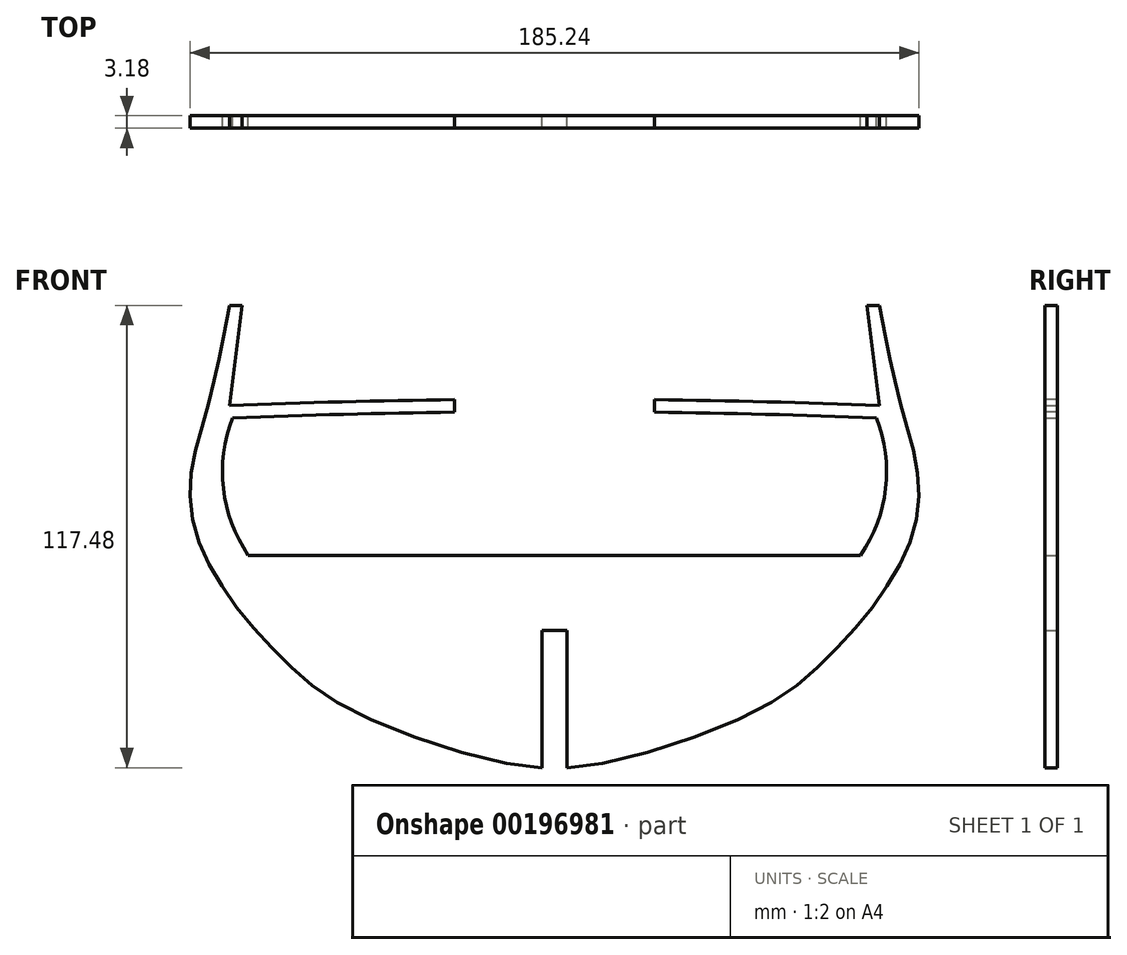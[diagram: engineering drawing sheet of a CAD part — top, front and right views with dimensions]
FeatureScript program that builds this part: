
annotation { "Feature Type Name" : "Feature", "Feature Type Description" : "" }
export const myFeature = defineFeature(function(context is Context, id is Id, definition is map)
    precondition{}
    {
        {
            var Q0;
            Q0=qCreatedBy(makeId("Front.planeOp"),FACE);
            var sketch = newSketch(context, id + "F0", { "sketchPlane" : qUnion([Q0])});
            skLineSegment(sketch, "E0", {"start": v(0, 0) * mm, "end": v(0, -53.97) * mm, "construction": true});
            skLineSegment(sketch, "E1", {"start": v(0, 0) * mm, "end": v(0, 34.93) * mm, "construction": true});
            skLineSegment(sketch, "E2", {"start": v(0, 34.93) * mm, "end": v(-81.76, 34.93) * mm, "construction": true});
            skLineSegment(sketch, "E3", {"start": v(0, 34.93) * mm, "end": v(81.76, 34.93) * mm, "construction": true});
            skLineSegment(sketch, "E4", {"start": v(81.76, 34.93) * mm, "end": v(88.9, 34.93) * mm, "construction": true});
            skLineSegment(sketch, "E5", {"start": v(0, 0) * mm, "end": v(77.79, 0) * mm});
            skLineSegment(sketch, "E6", {"start": v(77.79, 0) * mm, "end": v(88.92, 0) * mm, "construction": true});
            skLineSegment(sketch, "E7", {"start": v(77.79, 0) * mm, "end": v(81.76, 34.93) * mm, "construction": true});
            skLineSegment(sketch, "E8", {"start": v(0, 0) * mm, "end": v(-77.79, 0) * mm});
            skLineSegment(sketch, "E9", {"start": v(-77.79, 0) * mm, "end": v(-81.76, 34.92) * mm, "construction": true});
            skLineSegment(sketch, "E10", {"start": v(-3.18, -53.98) * mm, "end": v(-3.18, -19.05) * mm});
            skLineSegment(sketch, "E11", {"start": v(-3.17, -19.05) * mm, "end": v(0, -19.05) * mm});
            skLineSegment(sketch, "E12", {"start": v(0, -19.05) * mm, "end": v(3.17, -19.05) * mm});
            skLineSegment(sketch, "E13", {"start": v(3.17, -19.05) * mm, "end": v(3.17, -53.98) * mm});
            skFitSpline(sketch, "E14", {"points": [v(3.18, -53.98) * mm, v(47.63, -41.27) * mm, v(66.68, -28.57) * mm, v(78.58, -15.88) * mm, v(87.31, -3.17) * mm, v(92.08, 9.52) * mm, v(92.08, 22.23) * mm, v(88.9, 34.93) * mm, v(85.73, 47.62) * mm, v(82.55, 63.5) * mm], "startDerivative": vector(165.75, 0) * mm, "endDerivative": vector(-45.2, 225.97) * mm});
            skArc(sketch, "E15", {"start": v(81.76, 34.93) * mm, "mid": v(0, 36.51) * mm, "end": v(-81.76, 34.93) * mm});
            skArc(sketch, "E16", {"start": v(82.55, 38.07) * mm, "mid": v(0, 39.69) * mm, "end": v(-82.55, 38.07) * mm});
            skLineSegment(sketch, "E17", {"start": v(3.17, -53.97) * mm, "end": v(-3.18, -53.97) * mm, "construction": true});
            skPoint(sketch, "E18", {"position": v(0, 36.51) * mm});
            skLineSegment(sketch, "E19", {"start": v(82.55, 38.07) * mm, "end": v(88.05, 38.07) * mm, "construction": true});
            skPoint(sketch, "E20", {"position": v(0, 39.69) * mm});
            skLineSegment(sketch, "E21", {"start": v(82.55, 38.07) * mm, "end": v(79.37, 63.5) * mm});
            skLineSegment(sketch, "E22", {"start": v(79.38, 63.5) * mm, "end": v(82.55, 63.5) * mm});
            skArc(sketch, "E23", {"start": v(-81.76, 34.92) * mm, "mid": v(-84.13, 16.97) * mm, "end": v(-77.79, 0) * mm});
            skArc(sketch, "E24", {"start": v(77.79, 0) * mm, "mid": v(84.13, 16.97) * mm, "end": v(81.76, 34.92) * mm});
            skLineSegment(sketch, "E25.MirrorCS", {"start": v(-82.55, 38.07) * mm, "end": v(-79.38, 63.5) * mm});
            skLineSegment(sketch, "E26.MirrorCS", {"start": v(-79.38, 63.5) * mm, "end": v(-82.55, 63.5) * mm});
            skFitSpline(sketch, "E27.MirrorCS", {"points": [v(-3.18, -53.98) * mm, v(-47.63, -41.27) * mm, v(-66.68, -28.57) * mm, v(-78.58, -15.88) * mm, v(-87.31, -3.17) * mm, v(-92.08, 9.52) * mm, v(-92.08, 22.23) * mm, v(-88.9, 34.93) * mm, v(-85.73, 47.62) * mm, v(-82.55, 63.5) * mm], "startDerivative": vector(-165.75, 0) * mm, "endDerivative": vector(45.2, 225.97) * mm});
            skSolve(sketch);
        }
        {
            var Q0;
            Q0=makeQuery(id+"F0.imprint","IMPRINT",FACE,{"disambiguationData":[TD([[makeQuery(id+"F0.imprint","IMPRINT",EDGE,{"derivedFrom":sQuery(id+"F0.wireOp",EDGE,"E5")}),-1.0]])]});
            extrude(context, id + "F1", {"entities" : qUnion([Q0]), "endBound" : BoundingType.SYMMETRIC, "depth" : 3.17 * mm});
        }
        {
            var Q0;
            Q0=makeQuery(id+"F1.opExtrude","CAP_FACE",FACE,{"disambiguationData":[OSD([sQuery(id+"F0.wireOp",EDGE,"E5"),sQuery(id+"F0.wireOp",EDGE,"E8"),sQuery(id+"F0.wireOp",EDGE,"E10"),sQuery(id+"F0.wireOp",EDGE,"E11"),sQuery(id+"F0.wireOp",EDGE,"E12"),sQuery(id+"F0.wireOp",EDGE,"E13"),sQuery(id+"F0.wireOp",EDGE,"E14"),sQuery(id+"F0.wireOp",EDGE,"E15"),sQuery(id+"F0.wireOp",EDGE,"E16"),sQuery(id+"F0.wireOp",EDGE,"E21"),sQuery(id+"F0.wireOp",EDGE,"E22"),sQuery(id+"F0.wireOp",EDGE,"E23"),sQuery(id+"F0.wireOp",EDGE,"E24"),sQuery(id+"F0.wireOp",EDGE,"E25.MirrorCS"),sQuery(id+"F0.wireOp",EDGE,"E26.MirrorCS"),sQuery(id+"F0.wireOp",EDGE,"E27.MirrorCS")])],"isStart":false});
            var sketch = newSketch(context, id + "F2", { "sketchPlane" : qUnion([Q0])});
            skLineSegment(sketch, "E28", {"start": v(-25.4, 39.53) * mm, "end": v(-25.4, 36.36) * mm});
            skLineSegment(sketch, "E29", {"start": v(-25.4, 36.36) * mm, "end": v(25.4, 36.36) * mm});
            skLineSegment(sketch, "E30", {"start": v(25.4, 36.36) * mm, "end": v(25.4, 39.53) * mm});
            skArc(sketch, "E31", {"start": v(25.4, 39.53) * mm, "mid": v(0, 39.69) * mm, "end": v(-25.4, 39.53) * mm});
            skLineSegment(sketch, "E32", {"start": v(0, 36.36) * mm, "end": v(0, 0) * mm});
            skSolve(sketch);
        }
        {
            var Q0;
            Q0 = qSketchRegion(id + "F2", true);
            extrude(context, id + "F3", {"entities" : qUnion([Q0]), "operationType" : NewBodyOperationType.REMOVE, "endBound" : BoundingType.THROUGH_ALL, "oppositeDirection" : true, "depth" : 25.4 * mm});
        }
    });
